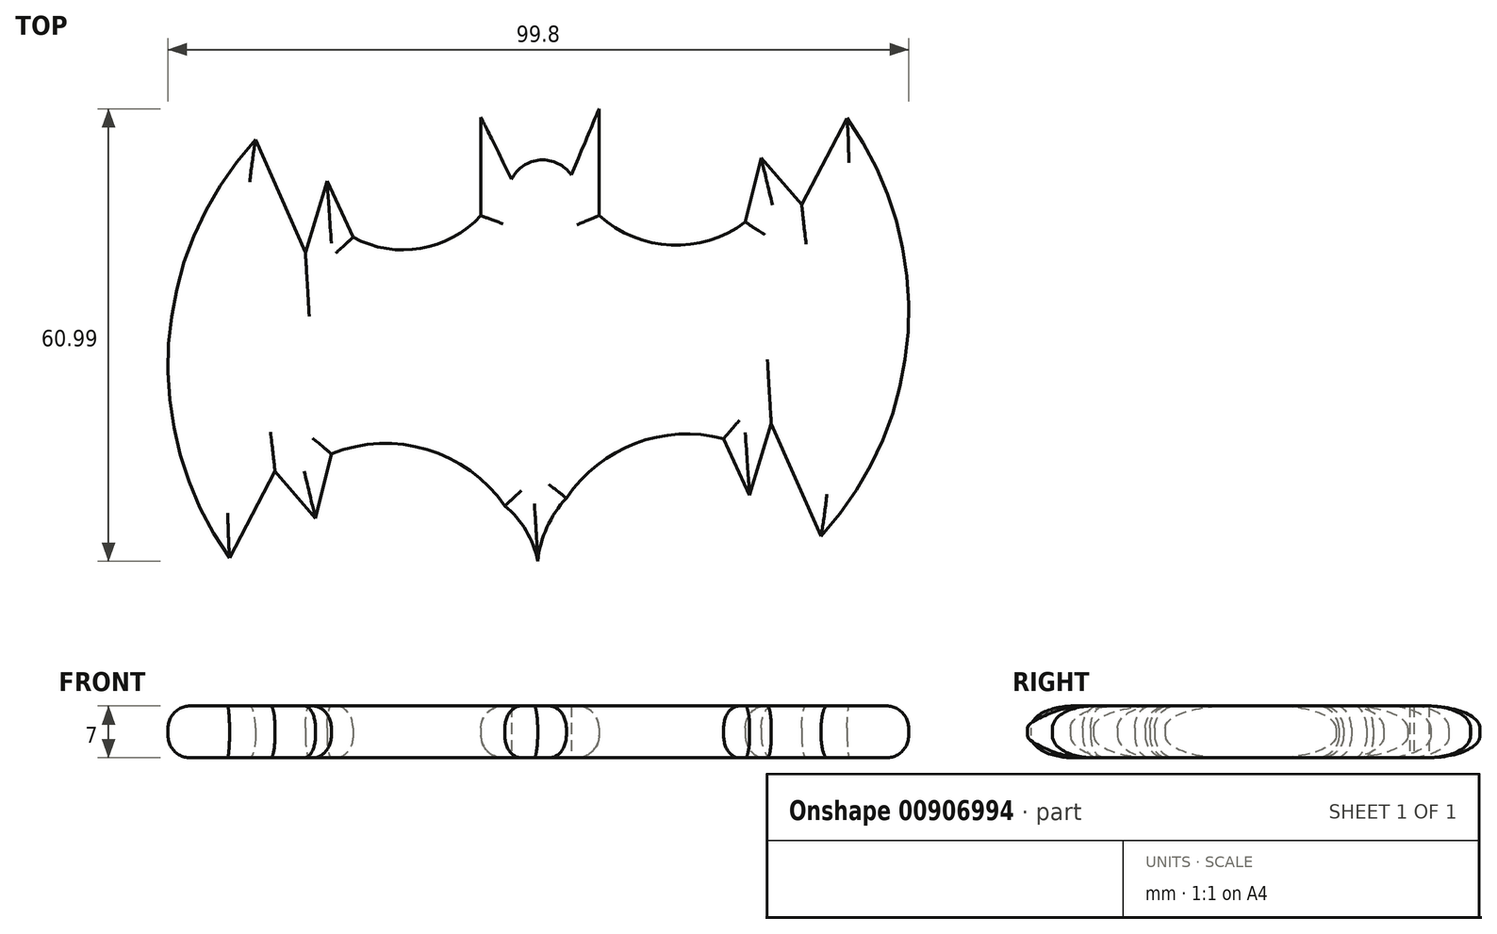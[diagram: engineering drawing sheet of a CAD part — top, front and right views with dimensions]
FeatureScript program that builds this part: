
annotation { "Feature Type Name" : "Feature", "Feature Type Description" : "" }
export const myFeature = defineFeature(function(context is Context, id is Id, definition is map)
    precondition{}
    {
        {
            var Q0;
            Q0=qCreatedBy(makeId("Top.planeOp"),FACE);
            var sketch = newSketch(context, id + "F0", { "sketchPlane" : qUnion([Q0])});
            skArc(sketch, "E0", {"start": v(-38.1, 26.72) * mm, "mid": v(-49.82, -0.84) * mm, "end": v(-41.61, -29.64) * mm});
            skArc(sketch, "E1.1.0", {"start": v(38.1, -26.72) * mm, "mid": v(49.82, 0.84) * mm, "end": v(41.61, 29.64) * mm});
            skPoint(sketch, "E1.center", {"position": v(0, 0) * mm});
            skLineSegment(sketch, "E2", {"start": v(-41.61, -29.64) * mm, "end": v(-35.48, -17.96) * mm});
            skLineSegment(sketch, "E3", {"start": v(-35.48, -17.96) * mm, "end": v(-35.48, -24.97) * mm});
            skArc(sketch, "E4", {"start": v(-4.53, -22.63) * mm, "mid": v(-14.98, -15.03) * mm, "end": v(-27.89, -15.62) * mm});
            skLineSegment(sketch, "E5.1.0", {"start": v(41.61, 29.64) * mm, "end": v(35.48, 17.96) * mm});
            skLineSegment(sketch, "E5.1.1", {"start": v(35.48, 17.96) * mm, "end": v(30.03, 24.29) * mm});
            skLineSegment(sketch, "E5.1.2", {"start": v(30.03, 24.29) * mm, "end": v(27.89, 15.62) * mm});
            skLineSegment(sketch, "E6", {"start": v(38.1, -26.72) * mm, "end": v(31.4, -11.53) * mm});
            skLineSegment(sketch, "E7", {"start": v(31.4, -11.53) * mm, "end": v(28.47, -21.17) * mm});
            skLineSegment(sketch, "E8", {"start": v(28.47, -21.17) * mm, "end": v(24.97, -13.58) * mm});
            skArc(sketch, "E9.1.0", {"start": v(-24.97, 13.58) * mm, "mid": v(-15.85, 12.08) * mm, "end": v(-7.74, 16.5) * mm});
            skLineSegment(sketch, "E9.1.2", {"start": v(-28.47, 21.17) * mm, "end": v(-24.97, 13.58) * mm});
            skLineSegment(sketch, "E9.1.4", {"start": v(-31.4, 11.53) * mm, "end": v(-28.47, 21.17) * mm});
            skLineSegment(sketch, "E9.1.5", {"start": v(-38.1, 26.72) * mm, "end": v(-31.4, 11.53) * mm});
            skArc(sketch, "E10", {"start": v(0, -34.06) * mm, "mid": v(-0.76, -27.75) * mm, "end": v(-4.53, -22.63) * mm});
            skArc(sketch, "E11.1.0", {"start": v(8.2, 16.53) * mm, "mid": v(17.88, 12.52) * mm, "end": v(27.89, 15.62) * mm});
            skLineSegment(sketch, "E12", {"start": v(-7.74, 16.5) * mm, "end": v(-7.74, 29.75) * mm});
            skLineSegment(sketch, "E13", {"start": v(-7.74, 29.75) * mm, "end": v(-3.6, 21.41) * mm});
            skLineSegment(sketch, "E14", {"start": v(8.2, 16.53) * mm, "end": v(8.2, 30.9) * mm});
            skLineSegment(sketch, "E15", {"start": v(8.2, 30.9) * mm, "end": v(4.45, 21.97) * mm});
            skArc(sketch, "E16", {"start": v(4.45, 21.97) * mm, "mid": v(0.27, 24) * mm, "end": v(-3.6, 21.41) * mm});
            skArc(sketch, "E17", {"start": v(24.97, -13.58) * mm, "mid": v(13.1, -14.2) * mm, "end": v(3.78, -21.57) * mm});
            skArc(sketch, "E18", {"start": v(3.78, -21.57) * mm, "mid": v(0.47, -27.38) * mm, "end": v(0, -34.06) * mm});
            skLineSegment(sketch, "E19.1.0", {"start": v(-35.48, -17.96) * mm, "end": v(-30.03, -24.29) * mm});
            skLineSegment(sketch, "E19.1.1", {"start": v(-30.03, -24.29) * mm, "end": v(-27.89, -15.62) * mm});
            skSolve(sketch);
        }
        {
            var Q0;
            Q0=makeQuery(id+"F0.imprint","IMPRINT",FACE,{"disambiguationData":[TD([[makeQuery(id+"F0.imprint","IMPRINT",EDGE,{"derivedFrom":sQuery(id+"F0.wireOp",EDGE,"X0qTVWh9-VfZW-o3Tf-exkY-fdIqOQphIt6q")}),-1.0]])]});
            var Q1;
            Q1=makeQuery(id+"F0.imprint","IMPRINT",FACE,{"disambiguationData":[TD([[makeQuery(id+"F0.imprint","IMPRINT",EDGE,{"derivedFrom":sQuery(id+"F0.wireOp",EDGE,"6iGZHZtX-1bip-HH5F-Ro9x-hsKvWLjZBWyp")}),-1.0]])]});
            var Q2;
            Q2=makeQuery(id+"F0.imprint","IMPRINT",FACE,{"disambiguationData":[TD([[makeQuery(id+"F0.imprint","IMPRINT",EDGE,{"derivedFrom":sQuery(id+"F0.wireOp",EDGE,"E0")}),1.0]])]});
            extrude(context, id + "F1", {"entities" : qUnion([Q0, Q1, Q2]), "depth" : 7 * mm, "offsetDistance" : 25 * mm});
        }
        {
            var Q0;
            Q0=makeQuery(id+"F1.opExtrude","CAP_EDGE",EDGE,{"disambiguationData":[OSD([sQuery(id+"F0.wireOp",EDGE,"E18")])],"isStart":false});
            var Q1;
            Q1=makeQuery(id+"F1.opExtrude","CAP_EDGE",EDGE,{"disambiguationData":[OSD([sQuery(id+"F0.wireOp",EDGE,"E17")])],"isStart":false});
            var Q2;
            Q2=makeQuery(id+"F1.opExtrude","CAP_EDGE",EDGE,{"disambiguationData":[OSD([sQuery(id+"F0.wireOp",EDGE,"E7")])],"isStart":false});
            var Q3;
            Q3=makeQuery(id+"F1.opExtrude","CAP_EDGE",EDGE,{"disambiguationData":[OSD([sQuery(id+"F0.wireOp",EDGE,"E1.1.0")])],"isStart":false});
            var Q4;
            Q4=makeQuery(id+"F1.opExtrude","CAP_EDGE",EDGE,{"disambiguationData":[OSD([sQuery(id+"F0.wireOp",EDGE,"E6")])],"isStart":false});
            var Q5;
            Q5=makeQuery(id+"F1.opExtrude","CAP_EDGE",EDGE,{"disambiguationData":[OSD([sQuery(id+"F0.wireOp",EDGE,"E5.1.0")])],"isStart":false});
            var Q6;
            Q6=makeQuery(id+"F1.opExtrude","CAP_EDGE",EDGE,{"disambiguationData":[OSD([sQuery(id+"F0.wireOp",EDGE,"E5.1.1")])],"isStart":false});
            var Q7;
            Q7=makeQuery(id+"F1.opExtrude","CAP_EDGE",EDGE,{"disambiguationData":[OSD([sQuery(id+"F0.wireOp",EDGE,"E5.1.2")])],"isStart":false});
            var Q8;
            Q8=makeQuery(id+"F1.opExtrude","CAP_EDGE",EDGE,{"disambiguationData":[OSD([sQuery(id+"F0.wireOp",EDGE,"E11.1.0")])],"isStart":false});
            var Q9;
            Q9=makeQuery(id+"F1.opExtrude","CAP_EDGE",EDGE,{"disambiguationData":[OSD([sQuery(id+"F0.wireOp",EDGE,"E14")])],"isStart":false});
            var Q10;
            Q10=makeQuery(id+"F1.opExtrude","CAP_EDGE",EDGE,{"disambiguationData":[OSD([sQuery(id+"F0.wireOp",EDGE,"E12")])],"isStart":false});
            var Q11;
            Q11=makeQuery(id+"F1.opExtrude","CAP_EDGE",EDGE,{"disambiguationData":[OSD([sQuery(id+"F0.wireOp",EDGE,"E9.1.0")])],"isStart":false});
            var Q12;
            Q12=makeQuery(id+"F1.opExtrude","CAP_EDGE",EDGE,{"disambiguationData":[OSD([sQuery(id+"F0.wireOp",EDGE,"E9.1.2")])],"isStart":false});
            var Q13;
            Q13=makeQuery(id+"F1.opExtrude","CAP_EDGE",EDGE,{"disambiguationData":[OSD([sQuery(id+"F0.wireOp",EDGE,"E9.1.5")])],"isStart":false});
            var Q14;
            Q14=makeQuery(id+"F1.opExtrude","CAP_EDGE",EDGE,{"disambiguationData":[OSD([sQuery(id+"F0.wireOp",EDGE,"E9.1.4")])],"isStart":false});
            var Q15;
            Q15=makeQuery(id+"F1.opExtrude","CAP_EDGE",EDGE,{"disambiguationData":[OSD([sQuery(id+"F0.wireOp",EDGE,"E0")])],"isStart":false});
            var Q16;
            Q16=makeQuery(id+"F1.opExtrude","CAP_EDGE",EDGE,{"disambiguationData":[OSD([sQuery(id+"F0.wireOp",EDGE,"E2")])],"isStart":false});
            var Q17;
            Q17=makeQuery(id+"F1.opExtrude","CAP_EDGE",EDGE,{"disambiguationData":[OSD([sQuery(id+"F0.wireOp",EDGE,"wEF84jsq-XExs-cQrN-D3yr-Ib7uIkRzdJAm")])],"isStart":false});
            var Q18;
            Q18=makeQuery(id+"F1.opExtrude","CAP_EDGE",EDGE,{"disambiguationData":[OSD([sQuery(id+"F0.wireOp",EDGE,"E10")])],"isStart":false});
            var Q19;
            Q19=makeQuery(id+"F1.opExtrude","CAP_EDGE",EDGE,{"disambiguationData":[OSD([sQuery(id+"F0.wireOp",EDGE,"E3")])],"isStart":false});
            var Q20;
            Q20=makeQuery(id+"F1.opExtrude","CAP_EDGE",EDGE,{"disambiguationData":[OSD([sQuery(id+"F0.wireOp",EDGE,"E8")])],"isStart":false});
            var Q21;
            Q21=makeQuery(id+"F1.opExtrude","CAP_EDGE",EDGE,{"disambiguationData":[OSD([sQuery(id+"F0.wireOp",EDGE,"E19.1.1")])],"isStart":false});
            var Q22;
            Q22=makeQuery(id+"F1.opExtrude","CAP_EDGE",EDGE,{"disambiguationData":[OSD([sQuery(id+"F0.wireOp",EDGE,"E4")])],"isStart":false});
            var Q23;
            Q23=makeQuery(id+"F1.opExtrude","CAP_EDGE",EDGE,{"disambiguationData":[OSD([sQuery(id+"F0.wireOp",EDGE,"E19.1.0")])],"isStart":false});
            var Q24;
            Q24=makeQuery(id+"F1.opExtrude","CAP_EDGE",EDGE,{"disambiguationData":[OSD([sQuery(id+"F0.wireOp",EDGE,"E1.1.0")])],"isStart":true});
            var Q25;
            Q25=makeQuery(id+"F1.opExtrude","CAP_EDGE",EDGE,{"disambiguationData":[OSD([sQuery(id+"F0.wireOp",EDGE,"E6")])],"isStart":true});
            var Q26;
            Q26=makeQuery(id+"F1.opExtrude","CAP_EDGE",EDGE,{"disambiguationData":[OSD([sQuery(id+"F0.wireOp",EDGE,"E7")])],"isStart":true});
            var Q27;
            Q27=makeQuery(id+"F1.opExtrude","CAP_EDGE",EDGE,{"disambiguationData":[OSD([sQuery(id+"F0.wireOp",EDGE,"E8")])],"isStart":true});
            var Q28;
            Q28=makeQuery(id+"F1.opExtrude","CAP_EDGE",EDGE,{"disambiguationData":[OSD([sQuery(id+"F0.wireOp",EDGE,"E17")])],"isStart":true});
            var Q29;
            Q29=makeQuery(id+"F1.opExtrude","CAP_EDGE",EDGE,{"disambiguationData":[OSD([sQuery(id+"F0.wireOp",EDGE,"E4")])],"isStart":true});
            var Q30;
            Q30=makeQuery(id+"F1.opExtrude","CAP_EDGE",EDGE,{"disambiguationData":[OSD([sQuery(id+"F0.wireOp",EDGE,"E10")])],"isStart":true});
            var Q31;
            Q31=makeQuery(id+"F1.opExtrude","CAP_EDGE",EDGE,{"disambiguationData":[OSD([sQuery(id+"F0.wireOp",EDGE,"E18")])],"isStart":true});
            var Q32;
            Q32=makeQuery(id+"F1.opExtrude","CAP_EDGE",EDGE,{"disambiguationData":[OSD([sQuery(id+"F0.wireOp",EDGE,"E19.1.1")])],"isStart":true});
            var Q33;
            Q33=makeQuery(id+"F1.opExtrude","CAP_EDGE",EDGE,{"disambiguationData":[OSD([sQuery(id+"F0.wireOp",EDGE,"E19.1.0")])],"isStart":true});
            var Q34;
            Q34=makeQuery(id+"F1.opExtrude","CAP_EDGE",EDGE,{"disambiguationData":[OSD([sQuery(id+"F0.wireOp",EDGE,"E2")])],"isStart":true});
            var Q35;
            Q35=makeQuery(id+"F1.opExtrude","CAP_EDGE",EDGE,{"disambiguationData":[OSD([sQuery(id+"F0.wireOp",EDGE,"E0")])],"isStart":true});
            var Q36;
            Q36=makeQuery(id+"F1.opExtrude","CAP_EDGE",EDGE,{"disambiguationData":[OSD([sQuery(id+"F0.wireOp",EDGE,"E9.1.5")])],"isStart":true});
            var Q37;
            Q37=makeQuery(id+"F1.opExtrude","CAP_EDGE",EDGE,{"disambiguationData":[OSD([sQuery(id+"F0.wireOp",EDGE,"E9.1.4")])],"isStart":true});
            var Q38;
            Q38=makeQuery(id+"F1.opExtrude","CAP_EDGE",EDGE,{"disambiguationData":[OSD([sQuery(id+"F0.wireOp",EDGE,"E12")])],"isStart":true});
            var Q39;
            Q39=makeQuery(id+"F1.opExtrude","CAP_EDGE",EDGE,{"disambiguationData":[OSD([sQuery(id+"F0.wireOp",EDGE,"E14")])],"isStart":true});
            var Q40;
            Q40=makeQuery(id+"F1.opExtrude","CAP_EDGE",EDGE,{"disambiguationData":[OSD([sQuery(id+"F0.wireOp",EDGE,"E11.1.0")])],"isStart":true});
            var Q41;
            Q41=makeQuery(id+"F1.opExtrude","CAP_EDGE",EDGE,{"disambiguationData":[OSD([sQuery(id+"F0.wireOp",EDGE,"E5.1.2")])],"isStart":true});
            var Q42;
            Q42=makeQuery(id+"F1.opExtrude","CAP_EDGE",EDGE,{"disambiguationData":[OSD([sQuery(id+"F0.wireOp",EDGE,"E5.1.1")])],"isStart":true});
            var Q43;
            Q43=makeQuery(id+"F1.opExtrude","CAP_EDGE",EDGE,{"disambiguationData":[OSD([sQuery(id+"F0.wireOp",EDGE,"E5.1.0")])],"isStart":true});
            var Q44;
            Q44=makeQuery(id+"F1.opExtrude","CAP_EDGE",EDGE,{"disambiguationData":[OSD([sQuery(id+"F0.wireOp",EDGE,"E9.1.0")])],"isStart":true});
            var Q45;
            Q45=makeQuery(id+"F1.opExtrude","CAP_EDGE",EDGE,{"disambiguationData":[OSD([sQuery(id+"F0.wireOp",EDGE,"E9.1.2")])],"isStart":true});
            fillet(context, id + "F2", {"entities" : qUnion([Q0, Q1, Q2, Q3, Q4, Q5, Q6, Q7, Q8, Q9, Q10, Q11, Q12, Q13, Q14, Q15, Q16, Q17, Q18, Q19, Q20, Q21, Q22, Q23, Q24, Q25, Q26, Q27, Q28, Q29, Q30, Q31, Q32, Q33, Q34, Q35, Q36, Q37, Q38, Q39, Q40, Q41, Q42, Q43, Q44, Q45]), "radius" : 3 * mm, "tangentPropagation" : true, "allowEdgeOverflow" : false});
        }
    });
